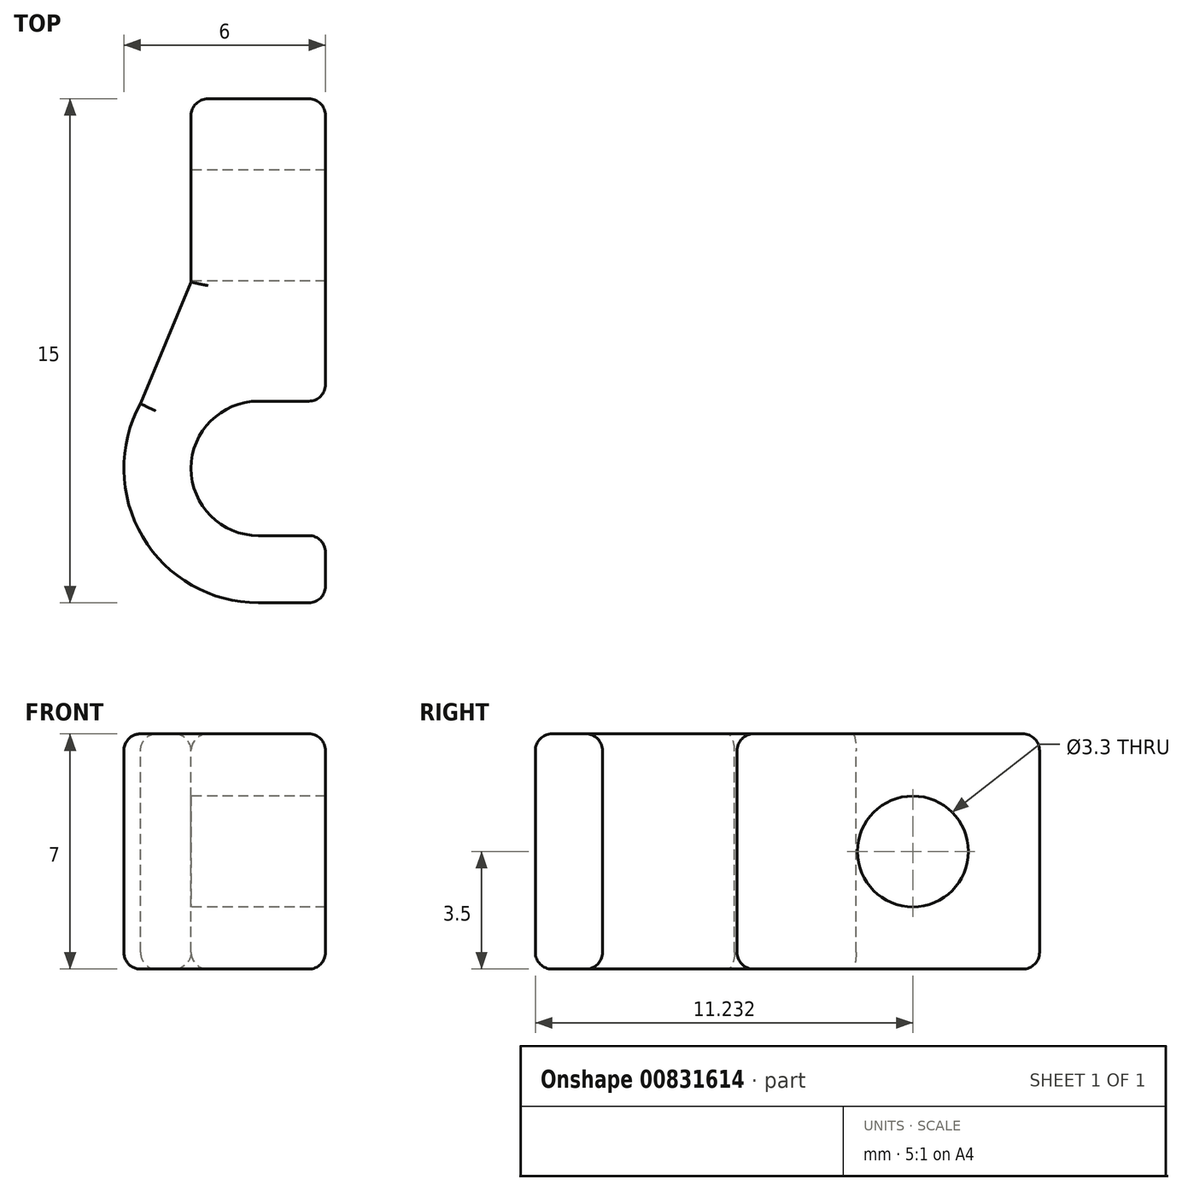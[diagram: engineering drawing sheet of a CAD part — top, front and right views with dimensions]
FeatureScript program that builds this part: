
annotation { "Feature Type Name" : "Feature", "Feature Type Description" : "" }
export const myFeature = defineFeature(function(context is Context, id is Id, definition is map)
    precondition{}
    {
        {
            var Q0;
            Q0=qCreatedBy(makeId("Right.planeOp"),FACE);
            var sketch = newSketch(context, id + "F0", { "sketchPlane" : qUnion([Q0])});
            skLineSegment(sketch, "E0.bottom", {"start": v(2, 3.5) * mm, "end": v(-2, 3.5) * mm, "construction": true});
            skLineSegment(sketch, "E0.top", {"start": v(2, -3.5) * mm, "end": v(-2, -3.5) * mm, "construction": true});
            skLineSegment(sketch, "E0.left", {"start": v(2, 3.5) * mm, "end": v(2, -3.5) * mm, "construction": true});
            skLineSegment(sketch, "E0.right", {"start": v(-2, 3.5) * mm, "end": v(-2, -3.5) * mm, "construction": true});
            skPoint(sketch, "E0.middle", {"position": v(0, 0) * mm});
            skLineSegment(sketch, "E1.bottom", {"start": v(-2, 3.5) * mm, "end": v(-4, 3.5) * mm});
            skLineSegment(sketch, "E1.top", {"start": v(-2, -3.5) * mm, "end": v(-4, -3.5) * mm});
            skLineSegment(sketch, "E1.left", {"start": v(-2, 3.5) * mm, "end": v(-2, -3.5) * mm});
            skLineSegment(sketch, "E1.right", {"start": v(-4, 3.5) * mm, "end": v(-4, -3.5) * mm});
            skLineSegment(sketch, "E2", {"start": v(0, 3.5) * mm, "end": v(0, -3.5) * mm, "construction": true});
            skSolve(sketch);
        }
        {
            var Q0;
            Q0=makeQuery(id+"F0.imprint","IMPRINT",FACE,{"disambiguationData":[TD([[makeQuery(id+"F0.imprint","IMPRINT",EDGE,{"derivedFrom":sQuery(id+"F0.wireOp",EDGE,"E1.bottom")}),1.0]])]});
            var Q1;
            Q1=sQuery(id+"F0.wireOp",EDGE,"E2");
            revolve(context, id + "F1", {"surfaceOperationType" : NewSurfaceOperationType.NEW, "entities" : qUnion([Q0]), "axis" : qUnion([Q1]), "revolveType" : RevolveType.ONE_DIRECTION, "angle" : 180 * degree});
        }
        {
            var Q0;
            Q0=makeQuery(id+"F1.opRevolve","CAP_FACE",FACE,{"disambiguationData":[OSD([sQuery(id+"F0.wireOp",EDGE,"E1.bottom"),sQuery(id+"F0.wireOp",EDGE,"E1.top"),sQuery(id+"F0.wireOp",EDGE,"E1.left"),sQuery(id+"F0.wireOp",EDGE,"E1.right")])],"isStart":false});
            var sketch = newSketch(context, id + "F2", { "sketchPlane" : qUnion([Q0])});
            skLineSegment(sketch, "E3.bottom", {"start": v(2, -3.5) * mm, "end": v(11, -3.5) * mm});
            skLineSegment(sketch, "E3.top", {"start": v(2, 3.5) * mm, "end": v(11, 3.5) * mm});
            skLineSegment(sketch, "E3.left", {"start": v(2, -3.5) * mm, "end": v(2, 3.5) * mm});
            skLineSegment(sketch, "E3.right", {"start": v(11, -3.5) * mm, "end": v(11, 3.5) * mm});
            skSolve(sketch);
        }
        {
            var Q0;
            Q0 = qSketchRegion(id + "F2", true);
            extrude(context, id + "F3", {"entities" : qUnion([Q0]), "operationType" : NewBodyOperationType.ADD, "oppositeDirection" : true, "depth" : 2 * mm, "offsetDistance" : 25 * mm});
        }
        {
            var Q0;
            Q0=makeQuery(id+"F3.opExtrude","CAP_FACE",FACE,{"disambiguationData":[OSD([sQuery(id+"F2.wireOp",EDGE,"E3.bottom"),sQuery(id+"F2.wireOp",EDGE,"E3.top"),sQuery(id+"F2.wireOp",EDGE,"E3.left"),sQuery(id+"F2.wireOp",EDGE,"E3.right")])],"isStart":false});
            var sketch = newSketch(context, id + "F4", { "sketchPlane" : qUnion([Q0])});
            skLineSegment(sketch, "E4", {"start": v(-3.46, 3.5) * mm, "end": v(-11, -3.5) * mm, "construction": true});
            skLineSegment(sketch, "E5", {"start": v(-11, -3.5) * mm, "end": v(-3.46, -3.5) * mm, "construction": true});
            skLineSegment(sketch, "E6", {"start": v(-3.46, -3.5) * mm, "end": v(-11, 3.5) * mm, "construction": true});
            skLineSegment(sketch, "E7", {"start": v(-11, 3.5) * mm, "end": v(-7.23, 0) * mm, "construction": true});
            skSolve(sketch);
        }
        {
            var Q0;
            Q0=sQuery(id+"F4.wireOp",VERTEX,"E7.end");
            var Q1;
            Q1=makeQuery(id+"F1.opRevolve","SWEPT_BODY",BODY,{"disambiguationData":[OSD([sQuery(id+"F0.wireOp",EDGE,"E1.bottom"),sQuery(id+"F0.wireOp",EDGE,"E1.top"),sQuery(id+"F0.wireOp",EDGE,"E1.left"),sQuery(id+"F0.wireOp",EDGE,"E1.right")])]});
            hole(context, id + "F5", {"style" : HoleStyle.SIMPLE, "endStyle" : HoleEndStyle.THROUGH, "standardTappedOrClearance" : lookupTablePath({ "fit" : "Normal", "standard" : "ISO", "size" : "M3", "type" : "Clearance" }), "standardBlindInLast" : lookupTablePath({ "fit" : "Standard", "standard" : "ISO", "size" : "M3", "type" : "Clearance" }), "holeDiameter" : 3.3 * mm, "majorDiameter" : 5 * mm, "isTappedThrough" : true, "tappedDepth" : 12 * mm, "tapClearance" : 3, "startFromSketch" : true, "locations" : qUnion([Q0]), "scope" : qUnion([Q1])});
        }
        {
            var Q0;
            Q0=makeQuery(id+"F3.boolean.opBoolean","INTERSECT",EDGE,{"derivedFrom":[makeQuery(id+"F1.opRevolve","SWEPT_FACE",FACE,{"disambiguationData":[OSD([sQuery(id+"F0.wireOp",EDGE,"E1.right")])]}),makeQuery(id+"F3.opExtrude","CAP_FACE",FACE,{"disambiguationData":[OSD([sQuery(id+"F2.wireOp",EDGE,"E3.bottom"),sQuery(id+"F2.wireOp",EDGE,"E3.top"),sQuery(id+"F2.wireOp",EDGE,"E3.left"),sQuery(id+"F2.wireOp",EDGE,"E3.right")])],"isStart":false})]});
            chamfer(context, id + "F6", {"entities" : qUnion([Q0]), "chamferType" : ChamferType.TWO_OFFSETS, "width1" : 5 * mm, "oppositeDirection" : false, "width2" : 4 * mm, "tangentPropagation" : true});
        }
        {
            var Q0;
            Q0=makeQuery(id+"F3.boolean.opBoolean","MERGE",FACE,{"derivedFrom":[makeQuery(id+"F1.opRevolve","CAP_FACE",FACE,{"disambiguationData":[OSD([sQuery(id+"F0.wireOp",EDGE,"E1.bottom"),sQuery(id+"F0.wireOp",EDGE,"E1.top"),sQuery(id+"F0.wireOp",EDGE,"E1.left"),sQuery(id+"F0.wireOp",EDGE,"E1.right")])],"isStart":false}),makeQuery(id+"F3.opExtrude","CAP_FACE",FACE,{"disambiguationData":[OSD([sQuery(id+"F2.wireOp",EDGE,"E3.bottom"),sQuery(id+"F2.wireOp",EDGE,"E3.top"),sQuery(id+"F2.wireOp",EDGE,"E3.left"),sQuery(id+"F2.wireOp",EDGE,"E3.right")])],"isStart":true})]});
            var Q1;
            Q1=makeQuery(id+"F1.opRevolve","CAP_FACE",FACE,{"disambiguationData":[OSD([sQuery(id+"F0.wireOp",EDGE,"E1.bottom"),sQuery(id+"F0.wireOp",EDGE,"E1.top"),sQuery(id+"F0.wireOp",EDGE,"E1.left"),sQuery(id+"F0.wireOp",EDGE,"E1.right")])],"isStart":true});
            extrude(context, id + "F7", {"entities" : qUnion([Q0, Q1]), "operationType" : NewBodyOperationType.ADD, "depth" : 2 * mm, "offsetDistance" : 25 * mm});
        }
        {
            var Q0;
            Q0=makeQuery(id+"F1.opRevolve","SWEPT_EDGE",EDGE,{"disambiguationData":[OSD([sQuery(id+"F0.wireOp",EDGE,"E1.bottom"),sQuery(id+"F0.wireOp",EDGE,"E1.left")])]});
            var Q1;
            Q1=makeQuery(id+"F1.opRevolve","CAP_EDGE",EDGE,{"disambiguationData":[OSD([sQuery(id+"F0.wireOp",EDGE,"E1.left")])],"isStart":true});
            var Q2;
            Q2=makeQuery(id+"F1.opRevolve","CAP_EDGE",EDGE,{"disambiguationData":[OSD([sQuery(id+"F0.wireOp",EDGE,"E1.left")])],"isStart":false});
            var Q3;
            Q3=makeQuery(id+"F1.opRevolve","SWEPT_EDGE",EDGE,{"disambiguationData":[OSD([sQuery(id+"F0.wireOp",EDGE,"E1.top"),sQuery(id+"F0.wireOp",EDGE,"E1.left")])]});
            var Q4;
            Q4=makeQuery(id+"F1.opRevolve","SWEPT_EDGE",EDGE,{"disambiguationData":[OSD([sQuery(id+"F0.wireOp",EDGE,"E1.bottom"),sQuery(id+"F0.wireOp",EDGE,"E1.right")])]});
            var Q5;
            {var subQ0=sQuery(id+"F2.wireOp",EDGE,"E3.top");Q5=makeQuery(id+"F6.opChamfer","BLEND_EDGE",EDGE,{"blendedFrom":[makeQuery(id+"F3.boolean.opBoolean","INTERSECT",EDGE,{"derivedFrom":[makeQuery(id+"F1.opRevolve","SWEPT_FACE",FACE,{"disambiguationData":[OSD([sQuery(id+"F0.wireOp",EDGE,"E1.right")])]}),makeQuery(id+"F3.opExtrude","CAP_FACE",FACE,{"disambiguationData":[OSD([sQuery(id+"F2.wireOp",EDGE,"E3.bottom"),subQ0,sQuery(id+"F2.wireOp",EDGE,"E3.left"),sQuery(id+"F2.wireOp",EDGE,"E3.right")])],"isStart":false})]}),makeQuery(id+"F3.boolean.opBoolean","MERGE",FACE,{"derivedFrom":[makeQuery(id+"F1.opRevolve","SWEPT_FACE",FACE,{"disambiguationData":[OSD([sQuery(id+"F0.wireOp",EDGE,"E1.bottom")])]}),makeQuery(id+"F3.opExtrude","SWEPT_FACE",FACE,{"disambiguationData":[OSD([subQ0])]})]})],"blendedInto":[makeQuery(id+"F3.boolean.opBoolean","MERGE",FACE,{"derivedFrom":[makeQuery(id+"F1.opRevolve","SWEPT_FACE",FACE,{"disambiguationData":[OSD([sQuery(id+"F0.wireOp",EDGE,"E1.bottom")])]}),makeQuery(id+"F3.opExtrude","SWEPT_FACE",FACE,{"disambiguationData":[OSD([subQ0])]})]})]});}
            var Q6;
            Q6=makeQuery(id+"F3.opExtrude","CAP_EDGE",EDGE,{"disambiguationData":[OSD([sQuery(id+"F2.wireOp",EDGE,"E3.top")])],"isStart":false});
            var Q7;
            Q7=makeQuery(id+"F3.opExtrude","CAP_EDGE",EDGE,{"disambiguationData":[OSD([sQuery(id+"F2.wireOp",EDGE,"E3.right")])],"isStart":false});
            var Q8;
            Q8=makeQuery(id+"F3.opExtrude","CAP_EDGE",EDGE,{"disambiguationData":[OSD([sQuery(id+"F2.wireOp",EDGE,"E3.bottom")])],"isStart":false});
            var Q9;
            Q9=makeQuery(id+"F1.opRevolve","SWEPT_EDGE",EDGE,{"disambiguationData":[OSD([sQuery(id+"F0.wireOp",EDGE,"E1.top"),sQuery(id+"F0.wireOp",EDGE,"E1.right")])]});
            var Q10;
            Q10=makeQuery(id+"F1.opRevolve","CAP_EDGE",EDGE,{"disambiguationData":[OSD([sQuery(id+"F0.wireOp",EDGE,"E1.right")])],"isStart":true});
            var Q11;
            {var subQ0=sQuery(id+"F2.wireOp",EDGE,"E3.bottom");Q11=makeQuery(id+"F6.opChamfer","BLEND_EDGE",EDGE,{"blendedFrom":[makeQuery(id+"F3.boolean.opBoolean","INTERSECT",EDGE,{"derivedFrom":[makeQuery(id+"F1.opRevolve","SWEPT_FACE",FACE,{"disambiguationData":[OSD([sQuery(id+"F0.wireOp",EDGE,"E1.right")])]}),makeQuery(id+"F3.opExtrude","CAP_FACE",FACE,{"disambiguationData":[OSD([subQ0,sQuery(id+"F2.wireOp",EDGE,"E3.top"),sQuery(id+"F2.wireOp",EDGE,"E3.left"),sQuery(id+"F2.wireOp",EDGE,"E3.right")])],"isStart":false})]}),makeQuery(id+"F3.boolean.opBoolean","MERGE",FACE,{"derivedFrom":[makeQuery(id+"F1.opRevolve","SWEPT_FACE",FACE,{"disambiguationData":[OSD([sQuery(id+"F0.wireOp",EDGE,"E1.top")])]}),makeQuery(id+"F3.opExtrude","SWEPT_FACE",FACE,{"disambiguationData":[OSD([subQ0])]})]})],"blendedInto":[makeQuery(id+"F3.boolean.opBoolean","MERGE",FACE,{"derivedFrom":[makeQuery(id+"F1.opRevolve","SWEPT_FACE",FACE,{"disambiguationData":[OSD([sQuery(id+"F0.wireOp",EDGE,"E1.top")])]}),makeQuery(id+"F3.opExtrude","SWEPT_FACE",FACE,{"disambiguationData":[OSD([subQ0])]})]})]});}
            var Q12;
            Q12=makeQuery(id+"F3.boolean.opBoolean","MERGE",EDGE,{"derivedFrom":[makeQuery(id+"F1.opRevolve","CAP_EDGE",EDGE,{"disambiguationData":[OSD([sQuery(id+"F0.wireOp",EDGE,"E1.top")])],"isStart":false}),makeQuery(id+"F3.opExtrude","CAP_EDGE",EDGE,{"disambiguationData":[OSD([sQuery(id+"F2.wireOp",EDGE,"E3.bottom")])],"isStart":true})]});
            var Q13;
            Q13=makeQuery(id+"F3.opExtrude","CAP_EDGE",EDGE,{"disambiguationData":[OSD([sQuery(id+"F2.wireOp",EDGE,"E3.right")])],"isStart":true});
            var Q14;
            Q14=makeQuery(id+"F3.boolean.opBoolean","MERGE",EDGE,{"derivedFrom":[makeQuery(id+"F1.opRevolve","CAP_EDGE",EDGE,{"disambiguationData":[OSD([sQuery(id+"F0.wireOp",EDGE,"E1.bottom")])],"isStart":false}),makeQuery(id+"F3.opExtrude","CAP_EDGE",EDGE,{"disambiguationData":[OSD([sQuery(id+"F2.wireOp",EDGE,"E3.top")])],"isStart":true})]});
            var Q15;
            Q15=makeQuery(id+"F3.opExtrude","SWEPT_EDGE",EDGE,{"disambiguationData":[OSD([sQuery(id+"F2.wireOp",EDGE,"E3.top"),sQuery(id+"F2.wireOp",EDGE,"E3.right")])]});
            var Q16;
            Q16=makeQuery(id+"F3.opExtrude","SWEPT_EDGE",EDGE,{"disambiguationData":[OSD([sQuery(id+"F2.wireOp",EDGE,"E3.bottom"),sQuery(id+"F2.wireOp",EDGE,"E3.right")])]});
            var Q17;
            Q17=makeQuery(id+"F7.opExtrude","CAP_EDGE",EDGE,{"disambiguationData":[OSD([sQuery(id+"F0.wireOp",EDGE,"E1.bottom"),sQuery(id+"F2.wireOp",EDGE,"E3.top")])],"isStart":false});
            var Q18;
            Q18=makeQuery(id+"F7.opExtrude","CAP_EDGE",EDGE,{"disambiguationData":[OSD([sQuery(id+"F2.wireOp",EDGE,"E3.right")])],"isStart":false});
            var Q19;
            Q19=makeQuery(id+"F7.opExtrude","CAP_EDGE",EDGE,{"disambiguationData":[OSD([sQuery(id+"F0.wireOp",EDGE,"E1.top"),sQuery(id+"F2.wireOp",EDGE,"E3.bottom")])],"isStart":false});
            var Q20;
            Q20=makeQuery(id+"F7.opExtrude","CAP_EDGE",EDGE,{"disambiguationData":[OSD([sQuery(id+"F0.wireOp",EDGE,"E1.top")])],"isStart":false});
            var Q21;
            {var subQ0=sQuery(id+"F0.wireOp",EDGE,"E1.left");Q21=makeQuery(id+"F7.opExtrude","CAP_EDGE",EDGE,{"disambiguationData":[OSD([subQ0]),TDD([makeQuery(id+"F1.opRevolve","CAP_EDGE",EDGE,{"disambiguationData":[OSD([subQ0])],"isStart":true})])],"isStart":false});}
            var Q22;
            Q22=makeQuery(id+"F7.opExtrude","CAP_EDGE",EDGE,{"disambiguationData":[OSD([sQuery(id+"F0.wireOp",EDGE,"E1.right")])],"isStart":false});
            var Q23;
            Q23=makeQuery(id+"F7.opExtrude","CAP_EDGE",EDGE,{"disambiguationData":[OSD([sQuery(id+"F0.wireOp",EDGE,"E1.bottom")])],"isStart":false});
            var Q24;
            {var subQ0=sQuery(id+"F0.wireOp",EDGE,"E1.left");Q24=makeQuery(id+"F7.opExtrude","CAP_EDGE",EDGE,{"disambiguationData":[OSD([subQ0]),TDD([makeQuery(id+"F1.opRevolve","CAP_EDGE",EDGE,{"disambiguationData":[OSD([subQ0])],"isStart":false})])],"isStart":false});}
            fillet(context, id + "F8", {"entities" : qUnion([Q0, Q1, Q2, Q3, Q4, Q5, Q6, Q7, Q8, Q9, Q10, Q11, Q12, Q13, Q14, Q15, Q16, Q17, Q18, Q19, Q20, Q21, Q22, Q23, Q24]), "radius" : 0.5 * mm, "tangentPropagation" : true, "allowEdgeOverflow" : false});
        }
    });
